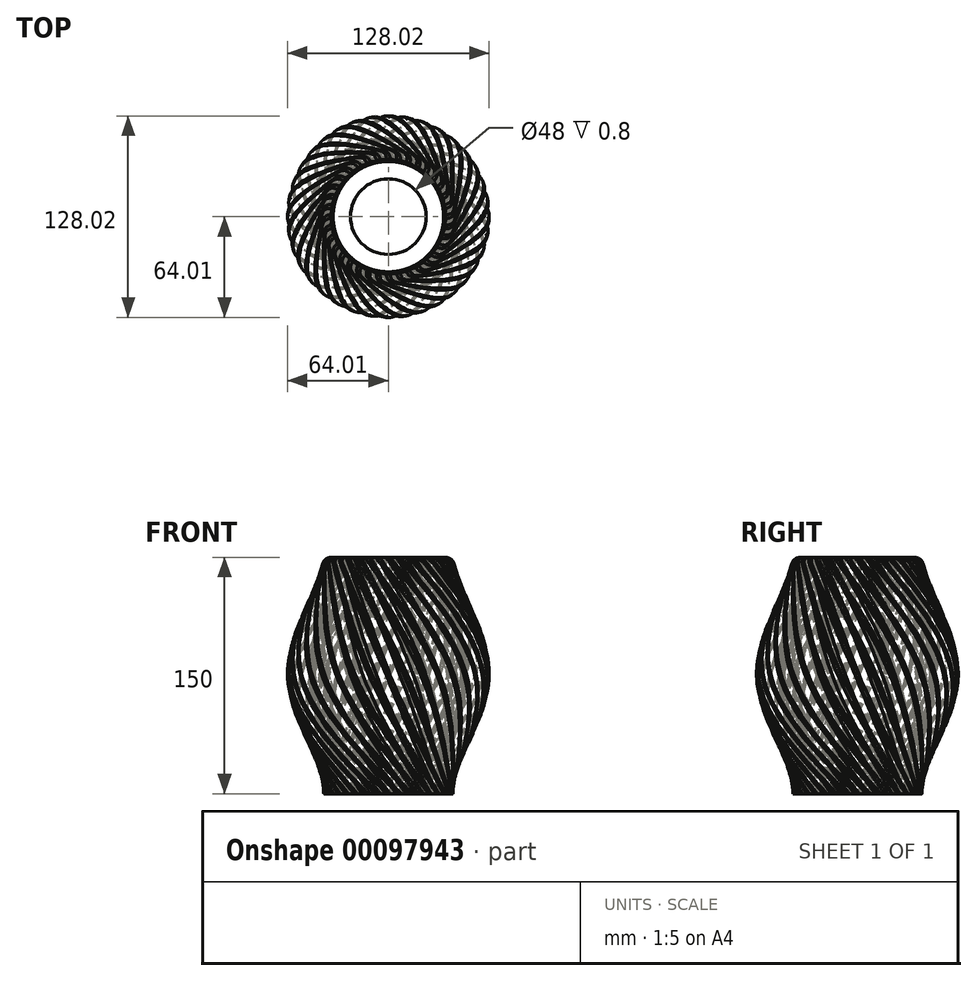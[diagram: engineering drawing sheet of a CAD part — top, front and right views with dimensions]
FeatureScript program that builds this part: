
annotation { "Feature Type Name" : "Feature", "Feature Type Description" : "" }
export const myFeature = defineFeature(function(context is Context, id is Id, definition is map)
    precondition{}
    {
        {
            var Q0;
            Q0=qCreatedBy(makeId("Top.planeOp"),FACE);
            var sketch = newSketch(context, id + "F0", { "sketchPlane" : qUnion([Q0])});
            skCircle(sketch, "E0", {"center": v(0, 0) * mm, "radius": 36 * mm, "construction": true});
            skCircle(sketch, "E1", {"center": v(0, 0) * mm, "radius": 41 * mm});
            skLineSegment(sketch, "E2", {"start": v(-40.98, 1.2) * mm, "end": v(-35.98, 1.2) * mm});
            skLineSegment(sketch, "E3", {"start": v(-40.98, -1.2) * mm, "end": v(-35.98, -1.2) * mm});
            skLineSegment(sketch, "E4.1.0", {"start": v(-40.57, -5.93) * mm, "end": v(-35.64, -5.07) * mm});
            skLineSegment(sketch, "E4.1.1", {"start": v(-40.15, -8.3) * mm, "end": v(-35.22, -7.43) * mm});
            skLineSegment(sketch, "E4.2.0", {"start": v(-38.92, -12.89) * mm, "end": v(-34.22, -11.18) * mm});
            skLineSegment(sketch, "E4.2.1", {"start": v(-38.1, -15.14) * mm, "end": v(-33.4, -13.43) * mm});
            skLineSegment(sketch, "E4.3.0", {"start": v(-36.1, -19.45) * mm, "end": v(-31.76, -16.95) * mm});
            skLineSegment(sketch, "E4.3.1", {"start": v(-34.9, -21.53) * mm, "end": v(-30.56, -19.03) * mm});
            skLineSegment(sketch, "E4.4.0", {"start": v(-32.17, -25.42) * mm, "end": v(-28.33, -22.2) * mm});
            skLineSegment(sketch, "E4.4.1", {"start": v(-30.62, -27.26) * mm, "end": v(-26.8, -24.05) * mm});
            skLineSegment(sketch, "E4.5.0", {"start": v(-27.26, -30.62) * mm, "end": v(-24.05, -26.8) * mm});
            skLineSegment(sketch, "E4.5.1", {"start": v(-25.42, -32.17) * mm, "end": v(-22.2, -28.33) * mm});
            skLineSegment(sketch, "E4.6.0", {"start": v(-21.53, -34.9) * mm, "end": v(-19.03, -30.56) * mm});
            skLineSegment(sketch, "E4.6.1", {"start": v(-19.45, -36.1) * mm, "end": v(-16.95, -31.76) * mm});
            skLineSegment(sketch, "E4.7.0", {"start": v(-15.14, -38.1) * mm, "end": v(-13.43, -33.4) * mm});
            skLineSegment(sketch, "E4.7.1", {"start": v(-12.89, -38.92) * mm, "end": v(-11.18, -34.22) * mm});
            skLineSegment(sketch, "E4.8.0", {"start": v(-8.3, -40.15) * mm, "end": v(-7.43, -35.22) * mm});
            skLineSegment(sketch, "E4.8.1", {"start": v(-5.93, -40.57) * mm, "end": v(-5.07, -35.64) * mm});
            skLineSegment(sketch, "E4.9.0", {"start": v(-1.2, -40.98) * mm, "end": v(-1.2, -35.98) * mm});
            skLineSegment(sketch, "E4.9.1", {"start": v(1.2, -40.98) * mm, "end": v(1.2, -35.98) * mm});
            skLineSegment(sketch, "E4.10.0", {"start": v(5.93, -40.57) * mm, "end": v(5.07, -35.64) * mm});
            skLineSegment(sketch, "E4.10.1", {"start": v(8.3, -40.15) * mm, "end": v(7.43, -35.22) * mm});
            skLineSegment(sketch, "E4.11.0", {"start": v(12.89, -38.92) * mm, "end": v(11.18, -34.22) * mm});
            skLineSegment(sketch, "E4.11.1", {"start": v(15.14, -38.1) * mm, "end": v(13.43, -33.4) * mm});
            skLineSegment(sketch, "E4.12.0", {"start": v(19.45, -36.1) * mm, "end": v(16.95, -31.76) * mm});
            skLineSegment(sketch, "E4.12.1", {"start": v(21.53, -34.9) * mm, "end": v(19.03, -30.56) * mm});
            skLineSegment(sketch, "E4.13.0", {"start": v(25.42, -32.17) * mm, "end": v(22.2, -28.33) * mm});
            skLineSegment(sketch, "E4.13.1", {"start": v(27.26, -30.62) * mm, "end": v(24.05, -26.8) * mm});
            skLineSegment(sketch, "E4.14.0", {"start": v(30.62, -27.26) * mm, "end": v(26.8, -24.05) * mm});
            skLineSegment(sketch, "E4.14.1", {"start": v(32.17, -25.42) * mm, "end": v(28.33, -22.2) * mm});
            skLineSegment(sketch, "E4.15.0", {"start": v(34.9, -21.53) * mm, "end": v(30.56, -19.03) * mm});
            skLineSegment(sketch, "E4.15.1", {"start": v(36.1, -19.45) * mm, "end": v(31.76, -16.95) * mm});
            skLineSegment(sketch, "E4.16.0", {"start": v(38.1, -15.14) * mm, "end": v(33.4, -13.43) * mm});
            skLineSegment(sketch, "E4.16.1", {"start": v(38.92, -12.89) * mm, "end": v(34.22, -11.18) * mm});
            skLineSegment(sketch, "E4.17.0", {"start": v(40.15, -8.3) * mm, "end": v(35.22, -7.43) * mm});
            skLineSegment(sketch, "E4.17.1", {"start": v(40.57, -5.93) * mm, "end": v(35.64, -5.07) * mm});
            skLineSegment(sketch, "E4.18.0", {"start": v(40.98, -1.2) * mm, "end": v(35.98, -1.2) * mm});
            skLineSegment(sketch, "E4.18.1", {"start": v(40.98, 1.2) * mm, "end": v(35.98, 1.2) * mm});
            skLineSegment(sketch, "E4.19.0", {"start": v(40.57, 5.93) * mm, "end": v(35.64, 5.07) * mm});
            skLineSegment(sketch, "E4.19.1", {"start": v(40.15, 8.3) * mm, "end": v(35.22, 7.43) * mm});
            skLineSegment(sketch, "E4.20.0", {"start": v(38.92, 12.89) * mm, "end": v(34.22, 11.18) * mm});
            skLineSegment(sketch, "E4.20.1", {"start": v(38.1, 15.14) * mm, "end": v(33.4, 13.43) * mm});
            skLineSegment(sketch, "E4.21.0", {"start": v(36.1, 19.45) * mm, "end": v(31.76, 16.95) * mm});
            skLineSegment(sketch, "E4.21.1", {"start": v(34.9, 21.53) * mm, "end": v(30.56, 19.03) * mm});
            skLineSegment(sketch, "E4.22.0", {"start": v(32.17, 25.42) * mm, "end": v(28.33, 22.2) * mm});
            skLineSegment(sketch, "E4.22.1", {"start": v(30.62, 27.26) * mm, "end": v(26.8, 24.05) * mm});
            skLineSegment(sketch, "E4.23.0", {"start": v(27.26, 30.62) * mm, "end": v(24.05, 26.8) * mm});
            skLineSegment(sketch, "E4.23.1", {"start": v(25.42, 32.17) * mm, "end": v(22.2, 28.33) * mm});
            skLineSegment(sketch, "E4.24.0", {"start": v(21.53, 34.9) * mm, "end": v(19.03, 30.56) * mm});
            skLineSegment(sketch, "E4.24.1", {"start": v(19.45, 36.1) * mm, "end": v(16.95, 31.76) * mm});
            skLineSegment(sketch, "E4.25.0", {"start": v(15.14, 38.1) * mm, "end": v(13.43, 33.4) * mm});
            skLineSegment(sketch, "E4.25.1", {"start": v(12.89, 38.92) * mm, "end": v(11.18, 34.22) * mm});
            skLineSegment(sketch, "E4.26.0", {"start": v(8.3, 40.15) * mm, "end": v(7.43, 35.22) * mm});
            skLineSegment(sketch, "E4.26.1", {"start": v(5.93, 40.57) * mm, "end": v(5.07, 35.64) * mm});
            skLineSegment(sketch, "E4.27.0", {"start": v(1.2, 40.98) * mm, "end": v(1.2, 35.98) * mm});
            skLineSegment(sketch, "E4.27.1", {"start": v(-1.2, 40.98) * mm, "end": v(-1.2, 35.98) * mm});
            skLineSegment(sketch, "E4.28.0", {"start": v(-5.93, 40.57) * mm, "end": v(-5.07, 35.64) * mm});
            skLineSegment(sketch, "E4.28.1", {"start": v(-8.3, 40.15) * mm, "end": v(-7.43, 35.22) * mm});
            skLineSegment(sketch, "E4.29.0", {"start": v(-12.89, 38.92) * mm, "end": v(-11.18, 34.22) * mm});
            skLineSegment(sketch, "E4.29.1", {"start": v(-15.14, 38.1) * mm, "end": v(-13.43, 33.4) * mm});
            skLineSegment(sketch, "E4.30.0", {"start": v(-19.45, 36.1) * mm, "end": v(-16.95, 31.76) * mm});
            skLineSegment(sketch, "E4.30.1", {"start": v(-21.53, 34.9) * mm, "end": v(-19.03, 30.56) * mm});
            skLineSegment(sketch, "E4.31.0", {"start": v(-25.42, 32.17) * mm, "end": v(-22.2, 28.33) * mm});
            skLineSegment(sketch, "E4.31.1", {"start": v(-27.26, 30.62) * mm, "end": v(-24.05, 26.8) * mm});
            skLineSegment(sketch, "E4.32.0", {"start": v(-30.62, 27.26) * mm, "end": v(-26.8, 24.05) * mm});
            skLineSegment(sketch, "E4.32.1", {"start": v(-32.17, 25.42) * mm, "end": v(-28.33, 22.2) * mm});
            skLineSegment(sketch, "E4.33.0", {"start": v(-34.9, 21.53) * mm, "end": v(-30.56, 19.03) * mm});
            skLineSegment(sketch, "E4.33.1", {"start": v(-36.1, 19.45) * mm, "end": v(-31.76, 16.95) * mm});
            skLineSegment(sketch, "E4.34.0", {"start": v(-38.1, 15.14) * mm, "end": v(-33.4, 13.43) * mm});
            skLineSegment(sketch, "E4.34.1", {"start": v(-38.92, 12.89) * mm, "end": v(-34.22, 11.18) * mm});
            skLineSegment(sketch, "E4.35.0", {"start": v(-40.15, 8.3) * mm, "end": v(-35.22, 7.43) * mm});
            skLineSegment(sketch, "E4.35.1", {"start": v(-40.57, 5.93) * mm, "end": v(-35.64, 5.07) * mm});
            skArc(sketch, "E5", {"start": v(-35.98, 1.2) * mm, "mid": v(-35.86, 3.14) * mm, "end": v(-35.64, 5.07) * mm});
            skArc(sketch, "E6.1.0", {"start": v(-35.64, -5.07) * mm, "mid": v(-35.86, -3.14) * mm, "end": v(-35.98, -1.2) * mm});
            skArc(sketch, "E6.2.0", {"start": v(-34.22, -11.18) * mm, "mid": v(-34.77, -9.32) * mm, "end": v(-35.22, -7.43) * mm});
            skArc(sketch, "E6.3.0", {"start": v(-31.76, -16.95) * mm, "mid": v(-32.63, -15.21) * mm, "end": v(-33.4, -13.43) * mm});
            skArc(sketch, "E6.4.0", {"start": v(-28.33, -22.2) * mm, "mid": v(-29.49, -20.65) * mm, "end": v(-30.56, -19.03) * mm});
            skArc(sketch, "E6.5.0", {"start": v(-24.05, -26.8) * mm, "mid": v(-25.46, -25.46) * mm, "end": v(-26.8, -24.05) * mm});
            skArc(sketch, "E6.6.0", {"start": v(-19.03, -30.56) * mm, "mid": v(-20.65, -29.49) * mm, "end": v(-22.2, -28.33) * mm});
            skArc(sketch, "E6.7.0", {"start": v(-13.43, -33.4) * mm, "mid": v(-15.21, -32.63) * mm, "end": v(-16.95, -31.76) * mm});
            skArc(sketch, "E6.8.0", {"start": v(-7.43, -35.22) * mm, "mid": v(-9.32, -34.77) * mm, "end": v(-11.18, -34.22) * mm});
            skArc(sketch, "E6.9.0", {"start": v(-1.2, -35.98) * mm, "mid": v(-3.14, -35.86) * mm, "end": v(-5.07, -35.64) * mm});
            skArc(sketch, "E6.10.0", {"start": v(5.07, -35.64) * mm, "mid": v(3.14, -35.86) * mm, "end": v(1.2, -35.98) * mm});
            skArc(sketch, "E6.11.0", {"start": v(11.18, -34.22) * mm, "mid": v(9.32, -34.77) * mm, "end": v(7.43, -35.22) * mm});
            skArc(sketch, "E6.12.0", {"start": v(16.95, -31.76) * mm, "mid": v(15.21, -32.63) * mm, "end": v(13.43, -33.4) * mm});
            skArc(sketch, "E6.13.0", {"start": v(22.2, -28.33) * mm, "mid": v(20.65, -29.49) * mm, "end": v(19.03, -30.56) * mm});
            skArc(sketch, "E6.14.0", {"start": v(26.8, -24.05) * mm, "mid": v(25.46, -25.46) * mm, "end": v(24.05, -26.8) * mm});
            skArc(sketch, "E6.15.0", {"start": v(30.56, -19.03) * mm, "mid": v(29.49, -20.65) * mm, "end": v(28.33, -22.2) * mm});
            skArc(sketch, "E6.16.0", {"start": v(33.4, -13.43) * mm, "mid": v(32.63, -15.21) * mm, "end": v(31.76, -16.95) * mm});
            skArc(sketch, "E6.17.0", {"start": v(35.22, -7.43) * mm, "mid": v(34.77, -9.32) * mm, "end": v(34.22, -11.18) * mm});
            skArc(sketch, "E6.18.0", {"start": v(35.98, -1.2) * mm, "mid": v(35.86, -3.14) * mm, "end": v(35.64, -5.07) * mm});
            skArc(sketch, "E6.19.0", {"start": v(35.64, 5.07) * mm, "mid": v(35.86, 3.14) * mm, "end": v(35.98, 1.2) * mm});
            skArc(sketch, "E6.20.0", {"start": v(34.22, 11.18) * mm, "mid": v(34.77, 9.32) * mm, "end": v(35.22, 7.43) * mm});
            skArc(sketch, "E6.21.0", {"start": v(31.76, 16.95) * mm, "mid": v(32.63, 15.21) * mm, "end": v(33.4, 13.43) * mm});
            skArc(sketch, "E6.22.0", {"start": v(28.33, 22.2) * mm, "mid": v(29.49, 20.65) * mm, "end": v(30.56, 19.03) * mm});
            skArc(sketch, "E6.23.0", {"start": v(24.05, 26.8) * mm, "mid": v(25.46, 25.46) * mm, "end": v(26.8, 24.05) * mm});
            skArc(sketch, "E6.24.0", {"start": v(19.03, 30.56) * mm, "mid": v(20.65, 29.49) * mm, "end": v(22.2, 28.33) * mm});
            skArc(sketch, "E6.25.0", {"start": v(13.43, 33.4) * mm, "mid": v(15.21, 32.63) * mm, "end": v(16.95, 31.76) * mm});
            skArc(sketch, "E6.26.0", {"start": v(7.43, 35.22) * mm, "mid": v(9.32, 34.77) * mm, "end": v(11.18, 34.22) * mm});
            skArc(sketch, "E6.27.0", {"start": v(1.2, 35.98) * mm, "mid": v(3.14, 35.86) * mm, "end": v(5.07, 35.64) * mm});
            skArc(sketch, "E6.28.0", {"start": v(-5.07, 35.64) * mm, "mid": v(-3.14, 35.86) * mm, "end": v(-1.2, 35.98) * mm});
            skArc(sketch, "E6.29.0", {"start": v(-11.18, 34.22) * mm, "mid": v(-9.32, 34.77) * mm, "end": v(-7.43, 35.22) * mm});
            skArc(sketch, "E6.30.0", {"start": v(-16.95, 31.76) * mm, "mid": v(-15.21, 32.63) * mm, "end": v(-13.43, 33.4) * mm});
            skArc(sketch, "E6.31.0", {"start": v(-22.2, 28.33) * mm, "mid": v(-20.65, 29.49) * mm, "end": v(-19.03, 30.56) * mm});
            skArc(sketch, "E6.32.0", {"start": v(-26.8, 24.05) * mm, "mid": v(-25.46, 25.46) * mm, "end": v(-24.05, 26.8) * mm});
            skArc(sketch, "E6.33.0", {"start": v(-30.56, 19.03) * mm, "mid": v(-29.49, 20.65) * mm, "end": v(-28.33, 22.2) * mm});
            skArc(sketch, "E6.34.0", {"start": v(-33.4, 13.43) * mm, "mid": v(-32.63, 15.21) * mm, "end": v(-31.76, 16.95) * mm});
            skArc(sketch, "E6.35.0", {"start": v(-35.22, 7.43) * mm, "mid": v(-34.77, 9.32) * mm, "end": v(-34.22, 11.18) * mm});
            skSolve(sketch);
        }
        {
            var Q0;
            Q0=qCreatedBy(makeId("Top.planeOp"),FACE);
            cPlane(context, id + "F1", {"entities" : qUnion([Q0]), "cplaneType" : CPlaneType.OFFSET, "offset" : 150 * mm, "width" : 150 * mm, "height" : 150 * mm});
        }
        {
            var Q0;
            Q0=qCreatedBy(makeId("Top.planeOp"),FACE);
            cPlane(context, id + "F2", {"entities" : qUnion([Q0]), "cplaneType" : CPlaneType.OFFSET, "offset" : 75 * mm, "width" : 150 * mm, "height" : 150 * mm});
        }
        {
            var Q0;
            Q0=qCreatedBy(id+"F2.planeOp",FACE);
            var sketch = newSketch(context, id + "F3", { "sketchPlane" : qUnion([Q0])});
            skCircle(sketch, "E7", {"center": v(0, 0) * mm, "radius": 64 * mm});
            skCircle(sketch, "E8", {"center": v(0, 0) * mm, "radius": 50 * mm, "construction": true});
            skLineSegment(sketch, "E9", {"start": v(-63.99, 1.2) * mm, "end": v(-49.99, 1.2) * mm});
            skLineSegment(sketch, "E10", {"start": v(-63.99, -1.2) * mm, "end": v(-49.99, -1.2) * mm});
            skLineSegment(sketch, "E11.1.0", {"start": v(-63.22, -9.93) * mm, "end": v(-49.43, -7.5) * mm});
            skLineSegment(sketch, "E11.1.1", {"start": v(-62.8, -12.3) * mm, "end": v(-49.02, -9.86) * mm});
            skLineSegment(sketch, "E11.2.0", {"start": v(-60.54, -20.76) * mm, "end": v(-47.38, -15.97) * mm});
            skLineSegment(sketch, "E11.2.1", {"start": v(-59.72, -23.01) * mm, "end": v(-46.56, -18.22) * mm});
            skLineSegment(sketch, "E11.3.0", {"start": v(-56.02, -30.96) * mm, "end": v(-43.89, -23.95) * mm});
            skLineSegment(sketch, "E11.3.1", {"start": v(-54.82, -33.03) * mm, "end": v(-42.69, -26.03) * mm});
            skLineSegment(sketch, "E11.4.0", {"start": v(-49.79, -40.21) * mm, "end": v(-39.06, -31.21) * mm});
            skLineSegment(sketch, "E11.4.1", {"start": v(-48.25, -42.05) * mm, "end": v(-37.52, -33.05) * mm});
            skLineSegment(sketch, "E11.5.0", {"start": v(-42.05, -48.25) * mm, "end": v(-33.05, -37.52) * mm});
            skLineSegment(sketch, "E11.5.1", {"start": v(-40.21, -49.79) * mm, "end": v(-31.21, -39.06) * mm});
            skLineSegment(sketch, "E11.6.0", {"start": v(-33.03, -54.82) * mm, "end": v(-26.03, -42.69) * mm});
            skLineSegment(sketch, "E11.6.1", {"start": v(-30.96, -56.02) * mm, "end": v(-23.95, -43.89) * mm});
            skLineSegment(sketch, "E11.7.0", {"start": v(-23.01, -59.72) * mm, "end": v(-18.22, -46.56) * mm});
            skLineSegment(sketch, "E11.7.1", {"start": v(-20.76, -60.54) * mm, "end": v(-15.97, -47.38) * mm});
            skLineSegment(sketch, "E11.8.0", {"start": v(-12.3, -62.8) * mm, "end": v(-9.86, -49.02) * mm});
            skLineSegment(sketch, "E11.8.1", {"start": v(-9.93, -63.22) * mm, "end": v(-7.5, -49.43) * mm});
            skLineSegment(sketch, "E11.9.0", {"start": v(-1.2, -63.99) * mm, "end": v(-1.2, -49.99) * mm});
            skLineSegment(sketch, "E11.9.1", {"start": v(1.2, -63.99) * mm, "end": v(1.2, -49.99) * mm});
            skLineSegment(sketch, "E11.10.0", {"start": v(9.93, -63.22) * mm, "end": v(7.5, -49.43) * mm});
            skLineSegment(sketch, "E11.10.1", {"start": v(12.3, -62.8) * mm, "end": v(9.86, -49.02) * mm});
            skLineSegment(sketch, "E11.11.0", {"start": v(20.76, -60.54) * mm, "end": v(15.97, -47.38) * mm});
            skLineSegment(sketch, "E11.11.1", {"start": v(23.01, -59.72) * mm, "end": v(18.22, -46.56) * mm});
            skLineSegment(sketch, "E11.12.0", {"start": v(30.96, -56.02) * mm, "end": v(23.95, -43.89) * mm});
            skLineSegment(sketch, "E11.12.1", {"start": v(33.03, -54.82) * mm, "end": v(26.03, -42.69) * mm});
            skLineSegment(sketch, "E11.13.0", {"start": v(40.21, -49.79) * mm, "end": v(31.21, -39.06) * mm});
            skLineSegment(sketch, "E11.13.1", {"start": v(42.05, -48.25) * mm, "end": v(33.05, -37.52) * mm});
            skLineSegment(sketch, "E11.14.0", {"start": v(48.25, -42.05) * mm, "end": v(37.52, -33.05) * mm});
            skLineSegment(sketch, "E11.14.1", {"start": v(49.79, -40.21) * mm, "end": v(39.06, -31.21) * mm});
            skLineSegment(sketch, "E11.15.0", {"start": v(54.82, -33.03) * mm, "end": v(42.69, -26.03) * mm});
            skLineSegment(sketch, "E11.15.1", {"start": v(56.02, -30.96) * mm, "end": v(43.89, -23.95) * mm});
            skLineSegment(sketch, "E11.16.0", {"start": v(59.72, -23.01) * mm, "end": v(46.56, -18.22) * mm});
            skLineSegment(sketch, "E11.16.1", {"start": v(60.54, -20.76) * mm, "end": v(47.38, -15.97) * mm});
            skLineSegment(sketch, "E11.17.0", {"start": v(62.8, -12.3) * mm, "end": v(49.02, -9.86) * mm});
            skLineSegment(sketch, "E11.17.1", {"start": v(63.22, -9.93) * mm, "end": v(49.43, -7.5) * mm});
            skLineSegment(sketch, "E11.18.0", {"start": v(63.99, -1.2) * mm, "end": v(49.99, -1.2) * mm});
            skLineSegment(sketch, "E11.18.1", {"start": v(63.99, 1.2) * mm, "end": v(49.99, 1.2) * mm});
            skLineSegment(sketch, "E11.19.0", {"start": v(63.22, 9.93) * mm, "end": v(49.43, 7.5) * mm});
            skLineSegment(sketch, "E11.19.1", {"start": v(62.8, 12.3) * mm, "end": v(49.02, 9.86) * mm});
            skLineSegment(sketch, "E11.20.0", {"start": v(60.54, 20.76) * mm, "end": v(47.38, 15.97) * mm});
            skLineSegment(sketch, "E11.20.1", {"start": v(59.72, 23.01) * mm, "end": v(46.56, 18.22) * mm});
            skLineSegment(sketch, "E11.21.0", {"start": v(56.02, 30.96) * mm, "end": v(43.89, 23.95) * mm});
            skLineSegment(sketch, "E11.21.1", {"start": v(54.82, 33.03) * mm, "end": v(42.69, 26.03) * mm});
            skLineSegment(sketch, "E11.22.0", {"start": v(49.79, 40.21) * mm, "end": v(39.06, 31.21) * mm});
            skLineSegment(sketch, "E11.22.1", {"start": v(48.25, 42.05) * mm, "end": v(37.52, 33.05) * mm});
            skLineSegment(sketch, "E11.23.0", {"start": v(42.05, 48.25) * mm, "end": v(33.05, 37.52) * mm});
            skLineSegment(sketch, "E11.23.1", {"start": v(40.21, 49.79) * mm, "end": v(31.21, 39.06) * mm});
            skLineSegment(sketch, "E11.24.0", {"start": v(33.03, 54.82) * mm, "end": v(26.03, 42.69) * mm});
            skLineSegment(sketch, "E11.24.1", {"start": v(30.96, 56.02) * mm, "end": v(23.95, 43.89) * mm});
            skLineSegment(sketch, "E11.25.0", {"start": v(23.01, 59.72) * mm, "end": v(18.22, 46.56) * mm});
            skLineSegment(sketch, "E11.25.1", {"start": v(20.76, 60.54) * mm, "end": v(15.97, 47.38) * mm});
            skLineSegment(sketch, "E11.26.0", {"start": v(12.3, 62.8) * mm, "end": v(9.86, 49.02) * mm});
            skLineSegment(sketch, "E11.26.1", {"start": v(9.93, 63.22) * mm, "end": v(7.5, 49.43) * mm});
            skLineSegment(sketch, "E11.27.0", {"start": v(1.2, 63.99) * mm, "end": v(1.2, 49.99) * mm});
            skLineSegment(sketch, "E11.27.1", {"start": v(-1.2, 63.99) * mm, "end": v(-1.2, 49.99) * mm});
            skLineSegment(sketch, "E11.28.0", {"start": v(-9.93, 63.22) * mm, "end": v(-7.5, 49.43) * mm});
            skLineSegment(sketch, "E11.28.1", {"start": v(-12.3, 62.8) * mm, "end": v(-9.86, 49.02) * mm});
            skLineSegment(sketch, "E11.29.0", {"start": v(-20.76, 60.54) * mm, "end": v(-15.97, 47.38) * mm});
            skLineSegment(sketch, "E11.29.1", {"start": v(-23.01, 59.72) * mm, "end": v(-18.22, 46.56) * mm});
            skLineSegment(sketch, "E11.30.0", {"start": v(-30.96, 56.02) * mm, "end": v(-23.95, 43.89) * mm});
            skLineSegment(sketch, "E11.30.1", {"start": v(-33.03, 54.82) * mm, "end": v(-26.03, 42.69) * mm});
            skLineSegment(sketch, "E11.31.0", {"start": v(-40.21, 49.79) * mm, "end": v(-31.21, 39.06) * mm});
            skLineSegment(sketch, "E11.31.1", {"start": v(-42.05, 48.25) * mm, "end": v(-33.05, 37.52) * mm});
            skLineSegment(sketch, "E11.32.0", {"start": v(-48.25, 42.05) * mm, "end": v(-37.52, 33.05) * mm});
            skLineSegment(sketch, "E11.32.1", {"start": v(-49.79, 40.21) * mm, "end": v(-39.06, 31.21) * mm});
            skLineSegment(sketch, "E11.33.0", {"start": v(-54.82, 33.03) * mm, "end": v(-42.69, 26.03) * mm});
            skLineSegment(sketch, "E11.33.1", {"start": v(-56.02, 30.96) * mm, "end": v(-43.89, 23.95) * mm});
            skLineSegment(sketch, "E11.34.0", {"start": v(-59.72, 23.01) * mm, "end": v(-46.56, 18.22) * mm});
            skLineSegment(sketch, "E11.34.1", {"start": v(-60.54, 20.76) * mm, "end": v(-47.38, 15.97) * mm});
            skLineSegment(sketch, "E11.35.0", {"start": v(-62.8, 12.3) * mm, "end": v(-49.02, 9.86) * mm});
            skLineSegment(sketch, "E11.35.1", {"start": v(-63.22, 9.93) * mm, "end": v(-49.43, 7.5) * mm});
            skArc(sketch, "E12", {"start": v(-49.99, 1.2) * mm, "mid": v(-49.8, 4.36) * mm, "end": v(-49.43, 7.5) * mm});
            skArc(sketch, "E13.1.0", {"start": v(-49.43, -7.5) * mm, "mid": v(-49.8, -4.36) * mm, "end": v(-49.99, -1.2) * mm});
            skArc(sketch, "E13.2.0", {"start": v(-47.38, -15.97) * mm, "mid": v(-48.3, -12.94) * mm, "end": v(-49.02, -9.86) * mm});
            skArc(sketch, "E13.3.0", {"start": v(-43.89, -23.95) * mm, "mid": v(-45.32, -21.13) * mm, "end": v(-46.56, -18.22) * mm});
            skArc(sketch, "E13.4.0", {"start": v(-39.06, -31.21) * mm, "mid": v(-40.96, -28.68) * mm, "end": v(-42.69, -26.03) * mm});
            skArc(sketch, "E13.5.0", {"start": v(-33.05, -37.52) * mm, "mid": v(-35.36, -35.36) * mm, "end": v(-37.52, -33.05) * mm});
            skArc(sketch, "E13.6.0", {"start": v(-26.03, -42.69) * mm, "mid": v(-28.68, -40.96) * mm, "end": v(-31.21, -39.06) * mm});
            skArc(sketch, "E13.7.0", {"start": v(-18.22, -46.56) * mm, "mid": v(-21.13, -45.32) * mm, "end": v(-23.95, -43.89) * mm});
            skArc(sketch, "E13.8.0", {"start": v(-9.86, -49.02) * mm, "mid": v(-12.94, -48.3) * mm, "end": v(-15.97, -47.38) * mm});
            skArc(sketch, "E13.9.0", {"start": v(-1.2, -49.99) * mm, "mid": v(-4.36, -49.8) * mm, "end": v(-7.5, -49.43) * mm});
            skArc(sketch, "E13.10.0", {"start": v(7.5, -49.43) * mm, "mid": v(4.36, -49.8) * mm, "end": v(1.2, -49.99) * mm});
            skArc(sketch, "E13.11.0", {"start": v(15.97, -47.38) * mm, "mid": v(12.94, -48.3) * mm, "end": v(9.86, -49.02) * mm});
            skArc(sketch, "E13.12.0", {"start": v(23.95, -43.89) * mm, "mid": v(21.13, -45.32) * mm, "end": v(18.22, -46.56) * mm});
            skArc(sketch, "E13.13.0", {"start": v(31.21, -39.06) * mm, "mid": v(28.68, -40.96) * mm, "end": v(26.03, -42.69) * mm});
            skArc(sketch, "E13.14.0", {"start": v(37.52, -33.05) * mm, "mid": v(35.36, -35.36) * mm, "end": v(33.05, -37.52) * mm});
            skArc(sketch, "E13.15.0", {"start": v(42.69, -26.03) * mm, "mid": v(40.96, -28.68) * mm, "end": v(39.06, -31.21) * mm});
            skArc(sketch, "E13.16.0", {"start": v(46.56, -18.22) * mm, "mid": v(45.32, -21.13) * mm, "end": v(43.89, -23.95) * mm});
            skArc(sketch, "E13.17.0", {"start": v(49.02, -9.86) * mm, "mid": v(48.3, -12.94) * mm, "end": v(47.38, -15.97) * mm});
            skArc(sketch, "E13.18.0", {"start": v(49.99, -1.2) * mm, "mid": v(49.8, -4.36) * mm, "end": v(49.43, -7.5) * mm});
            skArc(sketch, "E13.19.0", {"start": v(49.43, 7.5) * mm, "mid": v(49.8, 4.36) * mm, "end": v(49.99, 1.2) * mm});
            skArc(sketch, "E13.20.0", {"start": v(47.38, 15.97) * mm, "mid": v(48.3, 12.94) * mm, "end": v(49.02, 9.86) * mm});
            skArc(sketch, "E13.21.0", {"start": v(43.89, 23.95) * mm, "mid": v(45.32, 21.13) * mm, "end": v(46.56, 18.22) * mm});
            skArc(sketch, "E13.22.0", {"start": v(39.06, 31.21) * mm, "mid": v(40.96, 28.68) * mm, "end": v(42.69, 26.03) * mm});
            skArc(sketch, "E13.23.0", {"start": v(33.05, 37.52) * mm, "mid": v(35.36, 35.36) * mm, "end": v(37.52, 33.05) * mm});
            skArc(sketch, "E13.24.0", {"start": v(26.03, 42.69) * mm, "mid": v(28.68, 40.96) * mm, "end": v(31.21, 39.06) * mm});
            skArc(sketch, "E13.25.0", {"start": v(18.22, 46.56) * mm, "mid": v(21.13, 45.32) * mm, "end": v(23.95, 43.89) * mm});
            skArc(sketch, "E13.26.0", {"start": v(9.86, 49.02) * mm, "mid": v(12.94, 48.3) * mm, "end": v(15.97, 47.38) * mm});
            skArc(sketch, "E13.27.0", {"start": v(1.2, 49.99) * mm, "mid": v(4.36, 49.8) * mm, "end": v(7.5, 49.43) * mm});
            skArc(sketch, "E13.28.0", {"start": v(-7.5, 49.43) * mm, "mid": v(-4.36, 49.8) * mm, "end": v(-1.2, 49.99) * mm});
            skArc(sketch, "E13.29.0", {"start": v(-15.97, 47.38) * mm, "mid": v(-12.94, 48.3) * mm, "end": v(-9.86, 49.02) * mm});
            skArc(sketch, "E13.30.0", {"start": v(-23.95, 43.89) * mm, "mid": v(-21.13, 45.32) * mm, "end": v(-18.22, 46.56) * mm});
            skArc(sketch, "E13.31.0", {"start": v(-31.21, 39.06) * mm, "mid": v(-28.68, 40.96) * mm, "end": v(-26.03, 42.69) * mm});
            skArc(sketch, "E13.32.0", {"start": v(-37.52, 33.05) * mm, "mid": v(-35.36, 35.36) * mm, "end": v(-33.05, 37.52) * mm});
            skArc(sketch, "E13.33.0", {"start": v(-42.69, 26.03) * mm, "mid": v(-40.96, 28.68) * mm, "end": v(-39.06, 31.21) * mm});
            skArc(sketch, "E13.34.0", {"start": v(-46.56, 18.22) * mm, "mid": v(-45.32, 21.13) * mm, "end": v(-43.89, 23.95) * mm});
            skArc(sketch, "E13.35.0", {"start": v(-49.02, 9.86) * mm, "mid": v(-48.3, 12.94) * mm, "end": v(-47.38, 15.97) * mm});
            skSolve(sketch);
        }
        {
            var Q0;
            Q0=qCreatedBy(id+"F1.planeOp",FACE);
            var sketch = newSketch(context, id + "F4", { "sketchPlane" : qUnion([Q0])});
            skCircle(sketch, "E14", {"center": v(0, 0) * mm, "radius": 36 * mm, "construction": true});
            skCircle(sketch, "E15", {"center": v(0, 0) * mm, "radius": 41 * mm});
            skLineSegment(sketch, "E16", {"start": v(-40.98, 1.2) * mm, "end": v(-35.98, 1.2) * mm});
            skLineSegment(sketch, "E17", {"start": v(-40.98, -1.2) * mm, "end": v(-35.98, -1.2) * mm});
            skLineSegment(sketch, "E18.1.0", {"start": v(-40.57, -5.93) * mm, "end": v(-35.64, -5.07) * mm});
            skLineSegment(sketch, "E18.1.1", {"start": v(-40.15, -8.3) * mm, "end": v(-35.22, -7.43) * mm});
            skLineSegment(sketch, "E18.2.0", {"start": v(-38.92, -12.89) * mm, "end": v(-34.22, -11.18) * mm});
            skLineSegment(sketch, "E18.2.1", {"start": v(-38.1, -15.14) * mm, "end": v(-33.4, -13.43) * mm});
            skLineSegment(sketch, "E18.3.0", {"start": v(-36.1, -19.45) * mm, "end": v(-31.76, -16.95) * mm});
            skLineSegment(sketch, "E18.3.1", {"start": v(-34.9, -21.53) * mm, "end": v(-30.56, -19.03) * mm});
            skLineSegment(sketch, "E18.4.0", {"start": v(-32.17, -25.42) * mm, "end": v(-28.33, -22.2) * mm});
            skLineSegment(sketch, "E18.4.1", {"start": v(-30.62, -27.26) * mm, "end": v(-26.8, -24.05) * mm});
            skLineSegment(sketch, "E18.5.0", {"start": v(-27.26, -30.62) * mm, "end": v(-24.05, -26.8) * mm});
            skLineSegment(sketch, "E18.5.1", {"start": v(-25.42, -32.17) * mm, "end": v(-22.2, -28.33) * mm});
            skLineSegment(sketch, "E18.6.0", {"start": v(-21.53, -34.9) * mm, "end": v(-19.03, -30.56) * mm});
            skLineSegment(sketch, "E18.6.1", {"start": v(-19.45, -36.1) * mm, "end": v(-16.95, -31.76) * mm});
            skLineSegment(sketch, "E18.7.0", {"start": v(-15.14, -38.1) * mm, "end": v(-13.43, -33.4) * mm});
            skLineSegment(sketch, "E18.7.1", {"start": v(-12.89, -38.92) * mm, "end": v(-11.18, -34.22) * mm});
            skLineSegment(sketch, "E18.8.0", {"start": v(-8.3, -40.15) * mm, "end": v(-7.43, -35.22) * mm});
            skLineSegment(sketch, "E18.8.1", {"start": v(-5.93, -40.57) * mm, "end": v(-5.07, -35.64) * mm});
            skLineSegment(sketch, "E18.9.0", {"start": v(-1.2, -40.98) * mm, "end": v(-1.2, -35.98) * mm});
            skLineSegment(sketch, "E18.9.1", {"start": v(1.2, -40.98) * mm, "end": v(1.2, -35.98) * mm});
            skLineSegment(sketch, "E18.10.0", {"start": v(5.93, -40.57) * mm, "end": v(5.07, -35.64) * mm});
            skLineSegment(sketch, "E18.10.1", {"start": v(8.3, -40.15) * mm, "end": v(7.43, -35.22) * mm});
            skLineSegment(sketch, "E18.11.0", {"start": v(12.89, -38.92) * mm, "end": v(11.18, -34.22) * mm});
            skLineSegment(sketch, "E18.11.1", {"start": v(15.14, -38.1) * mm, "end": v(13.43, -33.4) * mm});
            skLineSegment(sketch, "E18.12.0", {"start": v(19.45, -36.1) * mm, "end": v(16.95, -31.76) * mm});
            skLineSegment(sketch, "E18.12.1", {"start": v(21.53, -34.9) * mm, "end": v(19.03, -30.56) * mm});
            skLineSegment(sketch, "E18.13.0", {"start": v(25.42, -32.17) * mm, "end": v(22.2, -28.33) * mm});
            skLineSegment(sketch, "E18.13.1", {"start": v(27.26, -30.62) * mm, "end": v(24.05, -26.8) * mm});
            skLineSegment(sketch, "E18.14.0", {"start": v(30.62, -27.26) * mm, "end": v(26.8, -24.05) * mm});
            skLineSegment(sketch, "E18.14.1", {"start": v(32.17, -25.42) * mm, "end": v(28.33, -22.2) * mm});
            skLineSegment(sketch, "E18.15.0", {"start": v(34.9, -21.53) * mm, "end": v(30.56, -19.03) * mm});
            skLineSegment(sketch, "E18.15.1", {"start": v(36.1, -19.45) * mm, "end": v(31.76, -16.95) * mm});
            skLineSegment(sketch, "E18.16.0", {"start": v(38.1, -15.14) * mm, "end": v(33.4, -13.43) * mm});
            skLineSegment(sketch, "E18.16.1", {"start": v(38.92, -12.89) * mm, "end": v(34.22, -11.18) * mm});
            skLineSegment(sketch, "E18.17.0", {"start": v(40.15, -8.3) * mm, "end": v(35.22, -7.43) * mm});
            skLineSegment(sketch, "E18.17.1", {"start": v(40.57, -5.93) * mm, "end": v(35.64, -5.07) * mm});
            skLineSegment(sketch, "E18.18.0", {"start": v(40.98, -1.2) * mm, "end": v(35.98, -1.2) * mm});
            skLineSegment(sketch, "E18.18.1", {"start": v(40.98, 1.2) * mm, "end": v(35.98, 1.2) * mm});
            skLineSegment(sketch, "E18.19.0", {"start": v(40.57, 5.93) * mm, "end": v(35.64, 5.07) * mm});
            skLineSegment(sketch, "E18.19.1", {"start": v(40.15, 8.3) * mm, "end": v(35.22, 7.43) * mm});
            skLineSegment(sketch, "E18.20.0", {"start": v(38.92, 12.89) * mm, "end": v(34.22, 11.18) * mm});
            skLineSegment(sketch, "E18.20.1", {"start": v(38.1, 15.14) * mm, "end": v(33.4, 13.43) * mm});
            skLineSegment(sketch, "E18.21.0", {"start": v(36.1, 19.45) * mm, "end": v(31.76, 16.95) * mm});
            skLineSegment(sketch, "E18.21.1", {"start": v(34.9, 21.53) * mm, "end": v(30.56, 19.03) * mm});
            skLineSegment(sketch, "E18.22.0", {"start": v(32.17, 25.42) * mm, "end": v(28.33, 22.2) * mm});
            skLineSegment(sketch, "E18.22.1", {"start": v(30.62, 27.26) * mm, "end": v(26.8, 24.05) * mm});
            skLineSegment(sketch, "E18.23.0", {"start": v(27.26, 30.62) * mm, "end": v(24.05, 26.8) * mm});
            skLineSegment(sketch, "E18.23.1", {"start": v(25.42, 32.17) * mm, "end": v(22.2, 28.33) * mm});
            skLineSegment(sketch, "E18.24.0", {"start": v(21.53, 34.9) * mm, "end": v(19.03, 30.56) * mm});
            skLineSegment(sketch, "E18.24.1", {"start": v(19.45, 36.1) * mm, "end": v(16.95, 31.76) * mm});
            skLineSegment(sketch, "E18.25.0", {"start": v(15.14, 38.1) * mm, "end": v(13.43, 33.4) * mm});
            skLineSegment(sketch, "E18.25.1", {"start": v(12.89, 38.92) * mm, "end": v(11.18, 34.22) * mm});
            skLineSegment(sketch, "E18.26.0", {"start": v(8.3, 40.15) * mm, "end": v(7.43, 35.22) * mm});
            skLineSegment(sketch, "E18.26.1", {"start": v(5.93, 40.57) * mm, "end": v(5.07, 35.64) * mm});
            skLineSegment(sketch, "E18.27.0", {"start": v(1.2, 40.98) * mm, "end": v(1.2, 35.98) * mm});
            skLineSegment(sketch, "E18.27.1", {"start": v(-1.2, 40.98) * mm, "end": v(-1.2, 35.98) * mm});
            skLineSegment(sketch, "E18.28.0", {"start": v(-5.93, 40.57) * mm, "end": v(-5.07, 35.64) * mm});
            skLineSegment(sketch, "E18.28.1", {"start": v(-8.3, 40.15) * mm, "end": v(-7.43, 35.22) * mm});
            skLineSegment(sketch, "E18.29.0", {"start": v(-12.89, 38.92) * mm, "end": v(-11.18, 34.22) * mm});
            skLineSegment(sketch, "E18.29.1", {"start": v(-15.14, 38.1) * mm, "end": v(-13.43, 33.4) * mm});
            skLineSegment(sketch, "E18.30.0", {"start": v(-19.45, 36.1) * mm, "end": v(-16.95, 31.76) * mm});
            skLineSegment(sketch, "E18.30.1", {"start": v(-21.53, 34.9) * mm, "end": v(-19.03, 30.56) * mm});
            skLineSegment(sketch, "E18.31.0", {"start": v(-25.42, 32.17) * mm, "end": v(-22.2, 28.33) * mm});
            skLineSegment(sketch, "E18.31.1", {"start": v(-27.26, 30.62) * mm, "end": v(-24.05, 26.8) * mm});
            skLineSegment(sketch, "E18.32.0", {"start": v(-30.62, 27.26) * mm, "end": v(-26.8, 24.05) * mm});
            skLineSegment(sketch, "E18.32.1", {"start": v(-32.17, 25.42) * mm, "end": v(-28.33, 22.2) * mm});
            skLineSegment(sketch, "E18.33.0", {"start": v(-34.9, 21.53) * mm, "end": v(-30.56, 19.03) * mm});
            skLineSegment(sketch, "E18.33.1", {"start": v(-36.1, 19.45) * mm, "end": v(-31.76, 16.95) * mm});
            skLineSegment(sketch, "E18.34.0", {"start": v(-38.1, 15.14) * mm, "end": v(-33.4, 13.43) * mm});
            skLineSegment(sketch, "E18.34.1", {"start": v(-38.92, 12.89) * mm, "end": v(-34.22, 11.18) * mm});
            skLineSegment(sketch, "E18.35.0", {"start": v(-40.15, 8.3) * mm, "end": v(-35.22, 7.43) * mm});
            skLineSegment(sketch, "E18.35.1", {"start": v(-40.57, 5.93) * mm, "end": v(-35.64, 5.07) * mm});
            skArc(sketch, "E19", {"start": v(-35.98, 1.2) * mm, "mid": v(-35.86, 3.14) * mm, "end": v(-35.64, 5.07) * mm});
            skArc(sketch, "E20.1.0", {"start": v(-35.64, -5.07) * mm, "mid": v(-35.86, -3.14) * mm, "end": v(-35.98, -1.2) * mm});
            skArc(sketch, "E20.2.0", {"start": v(-34.22, -11.18) * mm, "mid": v(-34.77, -9.32) * mm, "end": v(-35.22, -7.43) * mm});
            skArc(sketch, "E20.3.0", {"start": v(-31.76, -16.95) * mm, "mid": v(-32.63, -15.21) * mm, "end": v(-33.4, -13.43) * mm});
            skArc(sketch, "E20.4.0", {"start": v(-28.33, -22.2) * mm, "mid": v(-29.49, -20.65) * mm, "end": v(-30.56, -19.03) * mm});
            skArc(sketch, "E20.5.0", {"start": v(-24.05, -26.8) * mm, "mid": v(-25.46, -25.46) * mm, "end": v(-26.8, -24.05) * mm});
            skArc(sketch, "E20.6.0", {"start": v(-19.03, -30.56) * mm, "mid": v(-20.65, -29.49) * mm, "end": v(-22.2, -28.33) * mm});
            skArc(sketch, "E20.7.0", {"start": v(-13.43, -33.4) * mm, "mid": v(-15.21, -32.63) * mm, "end": v(-16.95, -31.76) * mm});
            skArc(sketch, "E20.8.0", {"start": v(-7.43, -35.22) * mm, "mid": v(-9.32, -34.77) * mm, "end": v(-11.18, -34.22) * mm});
            skArc(sketch, "E20.9.0", {"start": v(-1.2, -35.98) * mm, "mid": v(-3.14, -35.86) * mm, "end": v(-5.07, -35.64) * mm});
            skArc(sketch, "E20.10.0", {"start": v(5.07, -35.64) * mm, "mid": v(3.14, -35.86) * mm, "end": v(1.2, -35.98) * mm});
            skArc(sketch, "E20.11.0", {"start": v(11.18, -34.22) * mm, "mid": v(9.32, -34.77) * mm, "end": v(7.43, -35.22) * mm});
            skArc(sketch, "E20.12.0", {"start": v(16.95, -31.76) * mm, "mid": v(15.21, -32.63) * mm, "end": v(13.43, -33.4) * mm});
            skArc(sketch, "E20.13.0", {"start": v(22.2, -28.33) * mm, "mid": v(20.65, -29.49) * mm, "end": v(19.03, -30.56) * mm});
            skArc(sketch, "E20.14.0", {"start": v(26.8, -24.05) * mm, "mid": v(25.46, -25.46) * mm, "end": v(24.05, -26.8) * mm});
            skArc(sketch, "E20.15.0", {"start": v(30.56, -19.03) * mm, "mid": v(29.49, -20.65) * mm, "end": v(28.33, -22.2) * mm});
            skArc(sketch, "E20.16.0", {"start": v(33.4, -13.43) * mm, "mid": v(32.63, -15.21) * mm, "end": v(31.76, -16.95) * mm});
            skArc(sketch, "E20.17.0", {"start": v(35.22, -7.43) * mm, "mid": v(34.77, -9.32) * mm, "end": v(34.22, -11.18) * mm});
            skArc(sketch, "E20.18.0", {"start": v(35.98, -1.2) * mm, "mid": v(35.86, -3.14) * mm, "end": v(35.64, -5.07) * mm});
            skArc(sketch, "E20.19.0", {"start": v(35.64, 5.07) * mm, "mid": v(35.86, 3.14) * mm, "end": v(35.98, 1.2) * mm});
            skArc(sketch, "E20.20.0", {"start": v(34.22, 11.18) * mm, "mid": v(34.77, 9.32) * mm, "end": v(35.22, 7.43) * mm});
            skArc(sketch, "E20.21.0", {"start": v(31.76, 16.95) * mm, "mid": v(32.63, 15.21) * mm, "end": v(33.4, 13.43) * mm});
            skArc(sketch, "E20.22.0", {"start": v(28.33, 22.2) * mm, "mid": v(29.49, 20.65) * mm, "end": v(30.56, 19.03) * mm});
            skArc(sketch, "E20.23.0", {"start": v(24.05, 26.8) * mm, "mid": v(25.46, 25.46) * mm, "end": v(26.8, 24.05) * mm});
            skArc(sketch, "E20.24.0", {"start": v(19.03, 30.56) * mm, "mid": v(20.65, 29.49) * mm, "end": v(22.2, 28.33) * mm});
            skArc(sketch, "E20.25.0", {"start": v(13.43, 33.4) * mm, "mid": v(15.21, 32.63) * mm, "end": v(16.95, 31.76) * mm});
            skArc(sketch, "E20.26.0", {"start": v(7.43, 35.22) * mm, "mid": v(9.32, 34.77) * mm, "end": v(11.18, 34.22) * mm});
            skArc(sketch, "E20.27.0", {"start": v(1.2, 35.98) * mm, "mid": v(3.14, 35.86) * mm, "end": v(5.07, 35.64) * mm});
            skArc(sketch, "E20.28.0", {"start": v(-5.07, 35.64) * mm, "mid": v(-3.14, 35.86) * mm, "end": v(-1.2, 35.98) * mm});
            skArc(sketch, "E20.29.0", {"start": v(-11.18, 34.22) * mm, "mid": v(-9.32, 34.77) * mm, "end": v(-7.43, 35.22) * mm});
            skArc(sketch, "E20.30.0", {"start": v(-16.95, 31.76) * mm, "mid": v(-15.21, 32.63) * mm, "end": v(-13.43, 33.4) * mm});
            skArc(sketch, "E20.31.0", {"start": v(-22.2, 28.33) * mm, "mid": v(-20.65, 29.49) * mm, "end": v(-19.03, 30.56) * mm});
            skArc(sketch, "E20.32.0", {"start": v(-26.8, 24.05) * mm, "mid": v(-25.46, 25.46) * mm, "end": v(-24.05, 26.8) * mm});
            skArc(sketch, "E20.33.0", {"start": v(-30.56, 19.03) * mm, "mid": v(-29.49, 20.65) * mm, "end": v(-28.33, 22.2) * mm});
            skArc(sketch, "E20.34.0", {"start": v(-33.4, 13.43) * mm, "mid": v(-32.63, 15.21) * mm, "end": v(-31.76, 16.95) * mm});
            skArc(sketch, "E20.35.0", {"start": v(-35.22, 7.43) * mm, "mid": v(-34.77, 9.32) * mm, "end": v(-34.22, 11.18) * mm});
            skSolve(sketch);
        }
        {
            var Q0;
            {var subQ58=sQuery(id+"F0.wireOp",EDGE,"E2");Q0=makeQuery(id+"F0.imprint","IMPRINT",FACE,{"disambiguationData":[TD([[makeQuery(id+"F0.imprint","IMPRINT",EDGE,{"derivedFrom":subQ58}),-1.0]])]});}
            var Q1;
            {var subQ9=sQuery(id+"F3.wireOp",EDGE,"E9");Q1=makeQuery(id+"F3.imprint","IMPRINT",FACE,{"disambiguationData":[TD([[makeQuery(id+"F3.imprint","IMPRINT",EDGE,{"derivedFrom":subQ9}),-1.0]])]});}
            var Q2;
            {var subQ30=sQuery(id+"F4.wireOp",EDGE,"E16");Q2=makeQuery(id+"F4.imprint","IMPRINT",FACE,{"disambiguationData":[TD([[makeQuery(id+"F4.imprint","IMPRINT",EDGE,{"derivedFrom":subQ30}),-1.0]])]});}
            var Q3;
            Q3=sQuery(id+"F0.wireOp",VERTEX,"E4.9.1.start");
            var Q4;
            Q4=sQuery(id+"F3.wireOp",VERTEX,"E11.3.1.start");
            var Q5;
            Q5=sQuery(id+"F4.wireOp",VERTEX,"E18.34.1.start");
            loft(context, id + "F5", {"sheetProfilesArray" : [{ "sheetProfileEntities" : qUnion([Q0]) }, { "sheetProfileEntities" : qUnion([Q1]) }, { "sheetProfileEntities" : qUnion([Q2]) }], "matchConnections" : true, "connections" : [{ "connectionEntities" : qUnion([Q3, Q4, Q5]), "connectionEdgeQueries" : qUnion([]), "connectionEdgeParameters" : [] }]});
        }
        {
            var Q0;
            Q0=makeQuery(id+"F5.opLoft","MID_CAP_EDGE",EDGE,{"disambiguationData":[OSD([sQuery(id+"F4.wireOp",EDGE,"E15"),sQuery(id+"F4.wireOp",EDGE,"E18.5.0"),sQuery(id+"F4.wireOp",EDGE,"E18.5.1")])],"capPos":2.0});
            var Q1;
            Q1=makeQuery(id+"F5.opLoft","MID_CAP_EDGE",EDGE,{"disambiguationData":[OSD([sQuery(id+"F4.wireOp",EDGE,"E15"),sQuery(id+"F4.wireOp",EDGE,"E18.4.0"),sQuery(id+"F4.wireOp",EDGE,"E18.4.1")])],"capPos":2.0});
            var Q2;
            Q2=makeQuery(id+"F5.opLoft","MID_CAP_EDGE",EDGE,{"disambiguationData":[OSD([sQuery(id+"F4.wireOp",EDGE,"E15"),sQuery(id+"F4.wireOp",EDGE,"E18.3.0"),sQuery(id+"F4.wireOp",EDGE,"E18.3.1")])],"capPos":2.0});
            var Q3;
            Q3=makeQuery(id+"F5.opLoft","MID_CAP_EDGE",EDGE,{"disambiguationData":[OSD([sQuery(id+"F4.wireOp",EDGE,"E15"),sQuery(id+"F4.wireOp",EDGE,"E18.2.0"),sQuery(id+"F4.wireOp",EDGE,"E18.2.1")])],"capPos":2.0});
            var Q4;
            Q4=makeQuery(id+"F5.opLoft","MID_CAP_EDGE",EDGE,{"disambiguationData":[OSD([sQuery(id+"F4.wireOp",EDGE,"E15"),sQuery(id+"F4.wireOp",EDGE,"E18.1.0"),sQuery(id+"F4.wireOp",EDGE,"E18.1.1")])],"capPos":2.0});
            var Q5;
            Q5=makeQuery(id+"F5.opLoft","MID_CAP_EDGE",EDGE,{"disambiguationData":[OSD([sQuery(id+"F4.wireOp",EDGE,"E15"),sQuery(id+"F4.wireOp",EDGE,"E16"),sQuery(id+"F4.wireOp",EDGE,"E17")])],"capPos":2.0});
            var Q6;
            Q6=makeQuery(id+"F5.opLoft","MID_CAP_EDGE",EDGE,{"disambiguationData":[OSD([sQuery(id+"F4.wireOp",EDGE,"E15"),sQuery(id+"F4.wireOp",EDGE,"E18.35.0"),sQuery(id+"F4.wireOp",EDGE,"E18.35.1")])],"capPos":2.0});
            var Q7;
            Q7=makeQuery(id+"F5.opLoft","MID_CAP_EDGE",EDGE,{"disambiguationData":[OSD([sQuery(id+"F4.wireOp",EDGE,"E15"),sQuery(id+"F4.wireOp",EDGE,"E18.34.0"),sQuery(id+"F4.wireOp",EDGE,"E18.34.1")])],"capPos":2.0});
            var Q8;
            Q8=makeQuery(id+"F5.opLoft","MID_CAP_EDGE",EDGE,{"disambiguationData":[OSD([sQuery(id+"F4.wireOp",EDGE,"E15"),sQuery(id+"F4.wireOp",EDGE,"E18.33.0"),sQuery(id+"F4.wireOp",EDGE,"E18.33.1")])],"capPos":2.0});
            var Q9;
            Q9=makeQuery(id+"F5.opLoft","MID_CAP_EDGE",EDGE,{"disambiguationData":[OSD([sQuery(id+"F4.wireOp",EDGE,"E15"),sQuery(id+"F4.wireOp",EDGE,"E18.32.0"),sQuery(id+"F4.wireOp",EDGE,"E18.32.1")])],"capPos":2.0});
            var Q10;
            Q10=makeQuery(id+"F5.opLoft","MID_CAP_EDGE",EDGE,{"disambiguationData":[OSD([sQuery(id+"F4.wireOp",EDGE,"E15"),sQuery(id+"F4.wireOp",EDGE,"E18.31.0"),sQuery(id+"F4.wireOp",EDGE,"E18.31.1")])],"capPos":2.0});
            var Q11;
            Q11=makeQuery(id+"F5.opLoft","MID_CAP_EDGE",EDGE,{"disambiguationData":[OSD([sQuery(id+"F4.wireOp",EDGE,"E15"),sQuery(id+"F4.wireOp",EDGE,"E18.6.0"),sQuery(id+"F4.wireOp",EDGE,"E18.6.1")])],"capPos":2.0});
            var Q12;
            Q12=makeQuery(id+"F5.opLoft","MID_CAP_EDGE",EDGE,{"disambiguationData":[OSD([sQuery(id+"F4.wireOp",EDGE,"E15"),sQuery(id+"F4.wireOp",EDGE,"E18.7.0"),sQuery(id+"F4.wireOp",EDGE,"E18.7.1")])],"capPos":2.0});
            var Q13;
            Q13=makeQuery(id+"F5.opLoft","MID_CAP_EDGE",EDGE,{"disambiguationData":[OSD([sQuery(id+"F4.wireOp",EDGE,"E15"),sQuery(id+"F4.wireOp",EDGE,"E18.8.0"),sQuery(id+"F4.wireOp",EDGE,"E18.8.1")])],"capPos":2.0});
            var Q14;
            Q14=makeQuery(id+"F5.opLoft","MID_CAP_EDGE",EDGE,{"disambiguationData":[OSD([sQuery(id+"F4.wireOp",EDGE,"E15"),sQuery(id+"F4.wireOp",EDGE,"E18.9.0"),sQuery(id+"F4.wireOp",EDGE,"E18.9.1")])],"capPos":2.0});
            var Q15;
            Q15=makeQuery(id+"F5.opLoft","MID_CAP_EDGE",EDGE,{"disambiguationData":[OSD([sQuery(id+"F4.wireOp",EDGE,"E15"),sQuery(id+"F4.wireOp",EDGE,"E18.10.0"),sQuery(id+"F4.wireOp",EDGE,"E18.10.1")])],"capPos":2.0});
            var Q16;
            Q16=makeQuery(id+"F5.opLoft","MID_CAP_EDGE",EDGE,{"disambiguationData":[OSD([sQuery(id+"F4.wireOp",EDGE,"E15"),sQuery(id+"F4.wireOp",EDGE,"E18.11.0"),sQuery(id+"F4.wireOp",EDGE,"E18.11.1")])],"capPos":2.0});
            var Q17;
            Q17=makeQuery(id+"F5.opLoft","MID_CAP_EDGE",EDGE,{"disambiguationData":[OSD([sQuery(id+"F4.wireOp",EDGE,"E15"),sQuery(id+"F4.wireOp",EDGE,"E18.12.0"),sQuery(id+"F4.wireOp",EDGE,"E18.12.1")])],"capPos":2.0});
            var Q18;
            Q18=makeQuery(id+"F5.opLoft","MID_CAP_EDGE",EDGE,{"disambiguationData":[OSD([sQuery(id+"F4.wireOp",EDGE,"E15"),sQuery(id+"F4.wireOp",EDGE,"E18.13.0"),sQuery(id+"F4.wireOp",EDGE,"E18.13.1")])],"capPos":2.0});
            var Q19;
            Q19=makeQuery(id+"F5.opLoft","MID_CAP_EDGE",EDGE,{"disambiguationData":[OSD([sQuery(id+"F4.wireOp",EDGE,"E15"),sQuery(id+"F4.wireOp",EDGE,"E18.14.0"),sQuery(id+"F4.wireOp",EDGE,"E18.14.1")])],"capPos":2.0});
            var Q20;
            Q20=makeQuery(id+"F5.opLoft","MID_CAP_EDGE",EDGE,{"disambiguationData":[OSD([sQuery(id+"F4.wireOp",EDGE,"E15"),sQuery(id+"F4.wireOp",EDGE,"E18.15.0"),sQuery(id+"F4.wireOp",EDGE,"E18.15.1")])],"capPos":2.0});
            var Q21;
            Q21=makeQuery(id+"F5.opLoft","MID_CAP_EDGE",EDGE,{"disambiguationData":[OSD([sQuery(id+"F4.wireOp",EDGE,"E15"),sQuery(id+"F4.wireOp",EDGE,"E18.16.0"),sQuery(id+"F4.wireOp",EDGE,"E18.16.1")])],"capPos":2.0});
            var Q22;
            Q22=makeQuery(id+"F5.opLoft","MID_CAP_EDGE",EDGE,{"disambiguationData":[OSD([sQuery(id+"F4.wireOp",EDGE,"E15"),sQuery(id+"F4.wireOp",EDGE,"E18.17.0"),sQuery(id+"F4.wireOp",EDGE,"E18.17.1")])],"capPos":2.0});
            var Q23;
            Q23=makeQuery(id+"F5.opLoft","MID_CAP_EDGE",EDGE,{"disambiguationData":[OSD([sQuery(id+"F4.wireOp",EDGE,"E15"),sQuery(id+"F4.wireOp",EDGE,"E18.18.0"),sQuery(id+"F4.wireOp",EDGE,"E18.18.1")])],"capPos":2.0});
            var Q24;
            Q24=makeQuery(id+"F5.opLoft","MID_CAP_EDGE",EDGE,{"disambiguationData":[OSD([sQuery(id+"F4.wireOp",EDGE,"E15"),sQuery(id+"F4.wireOp",EDGE,"E18.19.0"),sQuery(id+"F4.wireOp",EDGE,"E18.19.1")])],"capPos":2.0});
            var Q25;
            Q25=makeQuery(id+"F5.opLoft","MID_CAP_EDGE",EDGE,{"disambiguationData":[OSD([sQuery(id+"F4.wireOp",EDGE,"E15"),sQuery(id+"F4.wireOp",EDGE,"E18.20.0"),sQuery(id+"F4.wireOp",EDGE,"E18.20.1")])],"capPos":2.0});
            var Q26;
            Q26=makeQuery(id+"F5.opLoft","MID_CAP_EDGE",EDGE,{"disambiguationData":[OSD([sQuery(id+"F4.wireOp",EDGE,"E15"),sQuery(id+"F4.wireOp",EDGE,"E18.21.0"),sQuery(id+"F4.wireOp",EDGE,"E18.21.1")])],"capPos":2.0});
            var Q27;
            Q27=makeQuery(id+"F5.opLoft","MID_CAP_EDGE",EDGE,{"disambiguationData":[OSD([sQuery(id+"F4.wireOp",EDGE,"E15"),sQuery(id+"F4.wireOp",EDGE,"E18.22.0"),sQuery(id+"F4.wireOp",EDGE,"E18.22.1")])],"capPos":2.0});
            var Q28;
            Q28=makeQuery(id+"F5.opLoft","MID_CAP_EDGE",EDGE,{"disambiguationData":[OSD([sQuery(id+"F4.wireOp",EDGE,"E15"),sQuery(id+"F4.wireOp",EDGE,"E18.23.0"),sQuery(id+"F4.wireOp",EDGE,"E18.23.1")])],"capPos":2.0});
            var Q29;
            Q29=makeQuery(id+"F5.opLoft","MID_CAP_EDGE",EDGE,{"disambiguationData":[OSD([sQuery(id+"F4.wireOp",EDGE,"E15"),sQuery(id+"F4.wireOp",EDGE,"E18.24.0"),sQuery(id+"F4.wireOp",EDGE,"E18.24.1")])],"capPos":2.0});
            var Q30;
            Q30=makeQuery(id+"F5.opLoft","MID_CAP_EDGE",EDGE,{"disambiguationData":[OSD([sQuery(id+"F4.wireOp",EDGE,"E15"),sQuery(id+"F4.wireOp",EDGE,"E18.30.0"),sQuery(id+"F4.wireOp",EDGE,"E18.30.1")])],"capPos":2.0});
            var Q31;
            Q31=makeQuery(id+"F5.opLoft","MID_CAP_EDGE",EDGE,{"disambiguationData":[OSD([sQuery(id+"F4.wireOp",EDGE,"E15"),sQuery(id+"F4.wireOp",EDGE,"E18.29.0"),sQuery(id+"F4.wireOp",EDGE,"E18.29.1")])],"capPos":2.0});
            var Q32;
            Q32=makeQuery(id+"F5.opLoft","MID_CAP_EDGE",EDGE,{"disambiguationData":[OSD([sQuery(id+"F4.wireOp",EDGE,"E15"),sQuery(id+"F4.wireOp",EDGE,"E18.28.0"),sQuery(id+"F4.wireOp",EDGE,"E18.28.1")])],"capPos":2.0});
            var Q33;
            Q33=makeQuery(id+"F5.opLoft","MID_CAP_EDGE",EDGE,{"disambiguationData":[OSD([sQuery(id+"F4.wireOp",EDGE,"E15"),sQuery(id+"F4.wireOp",EDGE,"E18.27.0"),sQuery(id+"F4.wireOp",EDGE,"E18.27.1")])],"capPos":2.0});
            var Q34;
            Q34=makeQuery(id+"F5.opLoft","MID_CAP_EDGE",EDGE,{"disambiguationData":[OSD([sQuery(id+"F4.wireOp",EDGE,"E15"),sQuery(id+"F4.wireOp",EDGE,"E18.26.0"),sQuery(id+"F4.wireOp",EDGE,"E18.26.1")])],"capPos":2.0});
            var Q35;
            Q35=makeQuery(id+"F5.opLoft","MID_CAP_EDGE",EDGE,{"disambiguationData":[OSD([sQuery(id+"F4.wireOp",EDGE,"E15"),sQuery(id+"F4.wireOp",EDGE,"E18.25.0"),sQuery(id+"F4.wireOp",EDGE,"E18.25.1")])],"capPos":2.0});
            fillet(context, id + "F6", {"entities" : qUnion([Q0, Q1, Q2, Q3, Q4, Q5, Q6, Q7, Q8, Q9, Q10, Q11, Q12, Q13, Q14, Q15, Q16, Q17, Q18, Q19, Q20, Q21, Q22, Q23, Q24, Q25, Q26, Q27, Q28, Q29, Q30, Q31, Q32, Q33, Q34, Q35]), "radius" : 5.6 * mm, "tangentPropagation" : true, "allowEdgeOverflow" : false});
        }
        {
            var Q0;
            {var subQ30=sQuery(id+"F4.wireOp",EDGE,"E16");Q0=makeQuery(id+"F5.opLoft","CAP_FACE",FACE,{"disambiguationData":[OSD([makeQuery(id+"F4.imprint","IMPRINT",FACE,{"disambiguationData":[TD([[makeQuery(id+"F4.imprint","IMPRINT",EDGE,{"derivedFrom":subQ30}),-1.0]])]})])],"isStart":true});}
            shell(context, id + "F7", {"entities" : qUnion([Q0]), "thickness" : .8 * mm});
        }
        {
            var Q0;
            {var subQ58=sQuery(id+"F0.wireOp",EDGE,"E2");Q0=makeQuery(id+"F5.opLoft","CAP_FACE",FACE,{"disambiguationData":[OSD([makeQuery(id+"F0.imprint","IMPRINT",FACE,{"disambiguationData":[TD([[makeQuery(id+"F0.imprint","IMPRINT",EDGE,{"derivedFrom":subQ58}),-1.0]])]})])],"isStart":true});}
            var sketch = newSketch(context, id + "F8", { "sketchPlane" : qUnion([Q0])});
            skCircle(sketch, "E21", {"center": v(0, 0) * mm, "radius": 24 * mm});
            skSolve(sketch);
        }
        {
            var Q0;
            Q0=makeQuery(id+"F8.imprint","IMPRINT",FACE,{"disambiguationData":[TD([[makeQuery(id+"F8.imprint","IMPRINT",EDGE,{"derivedFrom":sQuery(id+"F8.wireOp",EDGE,"E21")}),1.0]])]});
            extrude(context, id + "F9", {"entities" : qUnion([Q0]), "operationType" : NewBodyOperationType.REMOVE, "oppositeDirection" : true, "depth" : 25 * mm});
        }
    });
